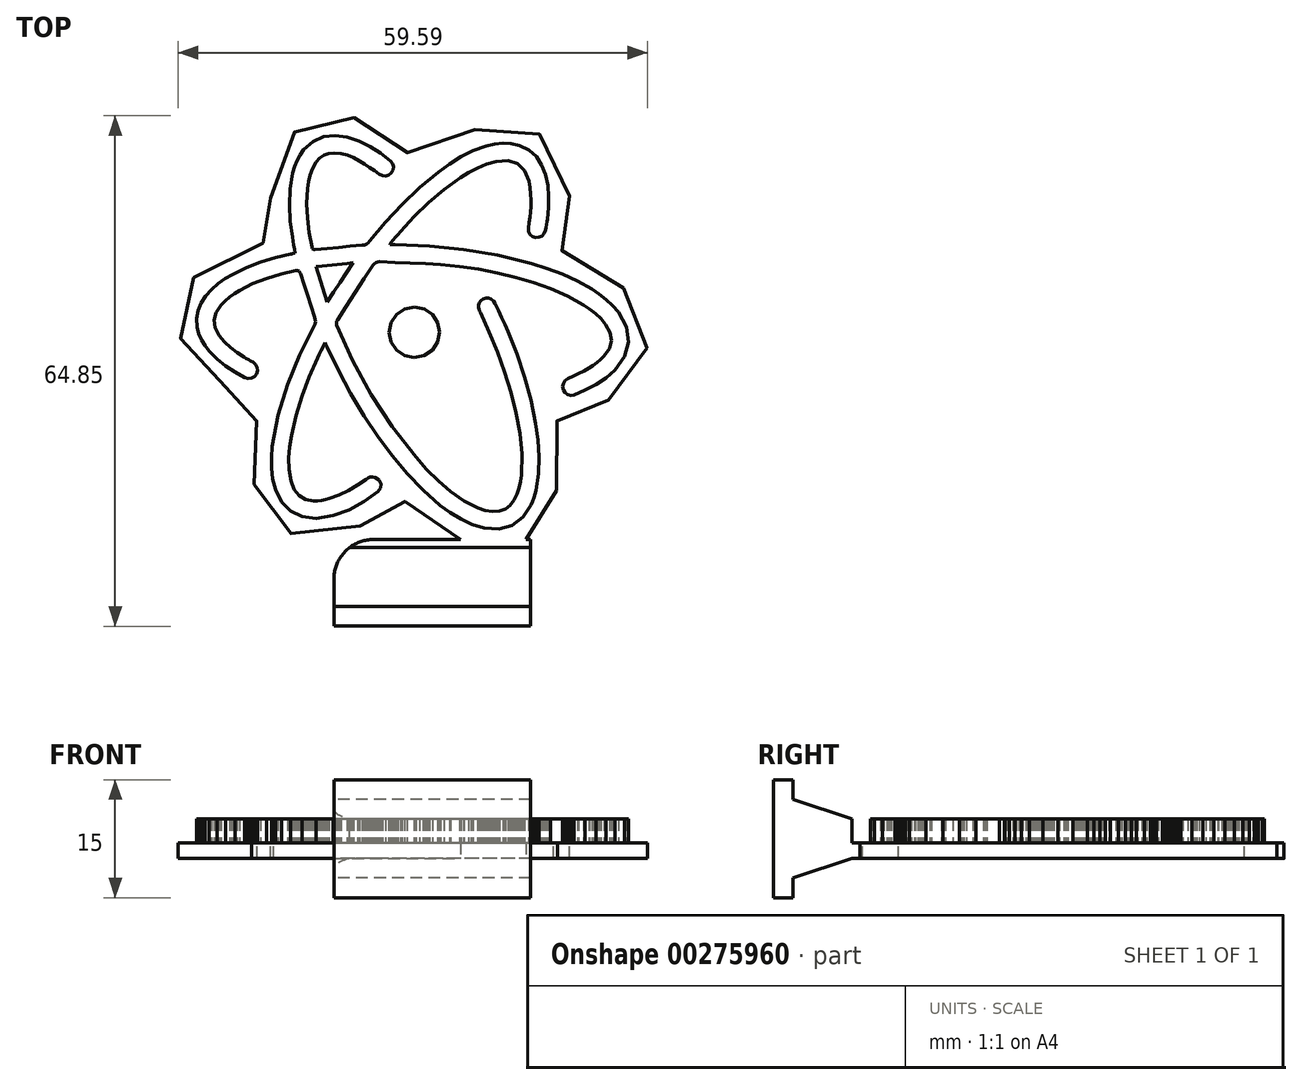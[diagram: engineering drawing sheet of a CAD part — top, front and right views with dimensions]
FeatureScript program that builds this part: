
annotation { "Feature Type Name" : "Feature", "Feature Type Description" : "" }
export const myFeature = defineFeature(function(context is Context, id is Id, definition is map)
    precondition{}
    {
        {
            var Q0;
            Q0=qCreatedBy(makeId("Top.planeOp"),FACE);
            var sketch = newSketch(context, id + "F0", { "sketchPlane" : qUnion([Q0])});
            skLineSegment(sketch, "E0", {"start": v(-11.14, -1.32) * mm, "end": v(-11.4, -1.85) * mm});
            skLineSegment(sketch, "E1", {"start": v(-11.4, -1.85) * mm, "end": v(-11.64, -2.35) * mm});
            skLineSegment(sketch, "E2", {"start": v(-11.64, -2.35) * mm, "end": v(-11.87, -2.83) * mm});
            skLineSegment(sketch, "E3", {"start": v(-11.87, -2.83) * mm, "end": v(-12.1, -3.3) * mm});
            skLineSegment(sketch, "E4", {"start": v(-12.1, -3.3) * mm, "end": v(-13.14, -5.69) * mm});
            skLineSegment(sketch, "E5", {"start": v(-13.14, -5.69) * mm, "end": v(-14.07, -8.11) * mm});
            skLineSegment(sketch, "E6", {"start": v(-14.07, -8.11) * mm, "end": v(-14.83, -10.59) * mm});
            skLineSegment(sketch, "E7", {"start": v(-14.83, -10.59) * mm, "end": v(-15.4, -13.13) * mm});
            skLineSegment(sketch, "E8", {"start": v(-15.4, -13.13) * mm, "end": v(-15.63, -14.56) * mm});
            skLineSegment(sketch, "E9", {"start": v(-15.63, -14.56) * mm, "end": v(-15.74, -16) * mm});
            skLineSegment(sketch, "E10", {"start": v(-15.74, -16) * mm, "end": v(-15.7, -17.44) * mm});
            skLineSegment(sketch, "E11", {"start": v(-15.7, -17.44) * mm, "end": v(-15.44, -18.87) * mm});
            skLineSegment(sketch, "E12", {"start": v(-15.44, -18.87) * mm, "end": v(-15.03, -19.96) * mm});
            skLineSegment(sketch, "E13", {"start": v(-15.03, -19.96) * mm, "end": v(-14.43, -20.74) * mm});
            skLineSegment(sketch, "E14", {"start": v(-14.43, -20.74) * mm, "end": v(-13.63, -21.24) * mm});
            skLineSegment(sketch, "E15", {"start": v(-13.63, -21.24) * mm, "end": v(-12.6, -21.43) * mm});
            skLineSegment(sketch, "E16", {"start": v(-12.6, -21.43) * mm, "end": v(-12.1, -21.43) * mm});
            skLineSegment(sketch, "E17", {"start": v(-12.1, -21.43) * mm, "end": v(-11.59, -21.37) * mm});
            skLineSegment(sketch, "E18", {"start": v(-11.59, -21.37) * mm, "end": v(-11.08, -21.27) * mm});
            skLineSegment(sketch, "E19", {"start": v(-11.08, -21.27) * mm, "end": v(-10.59, -21.14) * mm});
            skLineSegment(sketch, "E20", {"start": v(-10.59, -21.14) * mm, "end": v(-9.34, -20.7) * mm});
            skLineSegment(sketch, "E21", {"start": v(-9.34, -20.7) * mm, "end": v(-8.15, -20.12) * mm});
            skLineSegment(sketch, "E22", {"start": v(-8.15, -20.12) * mm, "end": v(-7.02, -19.44) * mm});
            skLineSegment(sketch, "E23", {"start": v(-7.02, -19.44) * mm, "end": v(-5.93, -18.7) * mm});
            skLineSegment(sketch, "E24", {"start": v(-5.93, -18.7) * mm, "end": v(-5.66, -18.53) * mm});
            skLineSegment(sketch, "E25", {"start": v(-5.66, -18.53) * mm, "end": v(-5.38, -18.42) * mm});
            skLineSegment(sketch, "E26", {"start": v(-5.38, -18.42) * mm, "end": v(-5.1, -18.39) * mm});
            skLineSegment(sketch, "E27", {"start": v(-5.1, -18.39) * mm, "end": v(-4.78, -18.46) * mm});
            skLineSegment(sketch, "E28", {"start": v(-4.78, -18.46) * mm, "end": v(-4.3, -18.8) * mm});
            skLineSegment(sketch, "E29", {"start": v(-4.3, -18.8) * mm, "end": v(-4.04, -19.28) * mm});
            skLineSegment(sketch, "E30", {"start": v(-4.04, -19.28) * mm, "end": v(-4.05, -19.81) * mm});
            skLineSegment(sketch, "E31", {"start": v(-4.05, -19.81) * mm, "end": v(-4.37, -20.26) * mm});
            skLineSegment(sketch, "E32", {"start": v(-4.37, -20.26) * mm, "end": v(-6.18, -21.52) * mm});
            skLineSegment(sketch, "E33", {"start": v(-6.18, -21.52) * mm, "end": v(-8.07, -22.57) * mm});
            skLineSegment(sketch, "E34", {"start": v(-8.07, -22.57) * mm, "end": v(-10.1, -23.32) * mm});
            skLineSegment(sketch, "E35", {"start": v(-10.1, -23.32) * mm, "end": v(-12.3, -23.63) * mm});
            skLineSegment(sketch, "E36", {"start": v(-12.3, -23.63) * mm, "end": v(-14.05, -23.43) * mm});
            skLineSegment(sketch, "E37", {"start": v(-14.05, -23.43) * mm, "end": v(-15.5, -22.73) * mm});
            skLineSegment(sketch, "E38", {"start": v(-15.5, -22.73) * mm, "end": v(-16.64, -21.57) * mm});
            skLineSegment(sketch, "E39", {"start": v(-16.64, -21.57) * mm, "end": v(-17.42, -19.98) * mm});
            skLineSegment(sketch, "E40", {"start": v(-17.42, -19.98) * mm, "end": v(-17.77, -18.63) * mm});
            skLineSegment(sketch, "E41", {"start": v(-17.77, -18.63) * mm, "end": v(-17.93, -17.27) * mm});
            skLineSegment(sketch, "E42", {"start": v(-17.93, -17.27) * mm, "end": v(-17.95, -15.9) * mm});
            skLineSegment(sketch, "E43", {"start": v(-17.95, -15.9) * mm, "end": v(-17.84, -14.52) * mm});
            skLineSegment(sketch, "E44", {"start": v(-17.84, -14.52) * mm, "end": v(-17.09, -10.5) * mm});
            skLineSegment(sketch, "E45", {"start": v(-17.09, -10.5) * mm, "end": v(-15.9, -6.63) * mm});
            skLineSegment(sketch, "E46", {"start": v(-15.9, -6.63) * mm, "end": v(-14.34, -2.89) * mm});
            skLineSegment(sketch, "E47", {"start": v(-14.34, -2.89) * mm, "end": v(-12.53, 0.76) * mm});
            skLineSegment(sketch, "E48", {"start": v(-12.53, 0.76) * mm, "end": v(-12.4, 1.06) * mm});
            skLineSegment(sketch, "E49", {"start": v(-12.4, 1.06) * mm, "end": v(-12.35, 1.35) * mm});
            skLineSegment(sketch, "E50", {"start": v(-12.35, 1.35) * mm, "end": v(-12.37, 1.64) * mm});
            skLineSegment(sketch, "E51", {"start": v(-12.37, 1.64) * mm, "end": v(-12.45, 1.95) * mm});
            skLineSegment(sketch, "E52", {"start": v(-12.45, 1.95) * mm, "end": v(-12.92, 3.32) * mm});
            skLineSegment(sketch, "E53", {"start": v(-12.92, 3.32) * mm, "end": v(-13.38, 4.7) * mm});
            skLineSegment(sketch, "E54", {"start": v(-13.38, 4.7) * mm, "end": v(-13.82, 6.07) * mm});
            skLineSegment(sketch, "E55", {"start": v(-13.82, 6.07) * mm, "end": v(-14.26, 7.45) * mm});
            skLineSegment(sketch, "E56", {"start": v(-14.26, 7.45) * mm, "end": v(-14.34, 7.66) * mm});
            skLineSegment(sketch, "E57", {"start": v(-14.34, 7.66) * mm, "end": v(-14.46, 7.8) * mm});
            skLineSegment(sketch, "E58", {"start": v(-14.46, 7.8) * mm, "end": v(-14.62, 7.84) * mm});
            skLineSegment(sketch, "E59", {"start": v(-14.62, 7.84) * mm, "end": v(-14.86, 7.81) * mm});
            skLineSegment(sketch, "E60", {"start": v(-14.86, 7.81) * mm, "end": v(-16.71, 7.37) * mm});
            skLineSegment(sketch, "E61", {"start": v(-16.71, 7.37) * mm, "end": v(-18.54, 6.84) * mm});
            skLineSegment(sketch, "E62", {"start": v(-18.54, 6.84) * mm, "end": v(-20.3, 6.16) * mm});
            skLineSegment(sketch, "E63", {"start": v(-20.3, 6.16) * mm, "end": v(-22, 5.29) * mm});
            skLineSegment(sketch, "E64", {"start": v(-22, 5.29) * mm, "end": v(-22.63, 4.89) * mm});
            skLineSegment(sketch, "E65", {"start": v(-22.63, 4.89) * mm, "end": v(-23.24, 4.44) * mm});
            skLineSegment(sketch, "E66", {"start": v(-23.24, 4.44) * mm, "end": v(-23.82, 3.96) * mm});
            skLineSegment(sketch, "E67", {"start": v(-23.82, 3.96) * mm, "end": v(-24.35, 3.44) * mm});
            skLineSegment(sketch, "E68", {"start": v(-24.35, 3.44) * mm, "end": v(-25, 2.53) * mm});
            skLineSegment(sketch, "E69", {"start": v(-25, 2.53) * mm, "end": v(-25.24, 1.57) * mm});
            skLineSegment(sketch, "E70", {"start": v(-25.24, 1.57) * mm, "end": v(-25.1, 0.59) * mm});
            skLineSegment(sketch, "E71", {"start": v(-25.1, 0.59) * mm, "end": v(-24.58, -0.42) * mm});
            skLineSegment(sketch, "E72", {"start": v(-24.58, -0.42) * mm, "end": v(-23.92, -1.25) * mm});
            skLineSegment(sketch, "E73", {"start": v(-23.92, -1.25) * mm, "end": v(-23.16, -1.96) * mm});
            skLineSegment(sketch, "E74", {"start": v(-23.16, -1.96) * mm, "end": v(-22.32, -2.58) * mm});
            skLineSegment(sketch, "E75", {"start": v(-22.32, -2.58) * mm, "end": v(-21.43, -3.15) * mm});
            skLineSegment(sketch, "E76", {"start": v(-21.43, -3.15) * mm, "end": v(-21.15, -3.32) * mm});
            skLineSegment(sketch, "E77", {"start": v(-21.15, -3.32) * mm, "end": v(-20.86, -3.48) * mm});
            skLineSegment(sketch, "E78", {"start": v(-20.86, -3.48) * mm, "end": v(-20.57, -3.64) * mm});
            skLineSegment(sketch, "E79", {"start": v(-20.57, -3.64) * mm, "end": v(-20.28, -3.8) * mm});
            skLineSegment(sketch, "E80", {"start": v(-20.28, -3.8) * mm, "end": v(-19.94, -4.1) * mm});
            skLineSegment(sketch, "E81", {"start": v(-19.94, -4.1) * mm, "end": v(-19.74, -4.48) * mm});
            skLineSegment(sketch, "E82", {"start": v(-19.74, -4.48) * mm, "end": v(-19.7, -4.89) * mm});
            skLineSegment(sketch, "E83", {"start": v(-19.7, -4.89) * mm, "end": v(-19.83, -5.3) * mm});
            skLineSegment(sketch, "E84", {"start": v(-19.83, -5.3) * mm, "end": v(-20.1, -5.64) * mm});
            skLineSegment(sketch, "E85", {"start": v(-20.1, -5.64) * mm, "end": v(-20.47, -5.83) * mm});
            skLineSegment(sketch, "E86", {"start": v(-20.47, -5.83) * mm, "end": v(-20.89, -5.88) * mm});
            skLineSegment(sketch, "E87", {"start": v(-20.89, -5.88) * mm, "end": v(-21.32, -5.75) * mm});
            skLineSegment(sketch, "E88", {"start": v(-21.32, -5.75) * mm, "end": v(-22.56, -5.06) * mm});
            skLineSegment(sketch, "E89", {"start": v(-22.56, -5.06) * mm, "end": v(-23.74, -4.3) * mm});
            skLineSegment(sketch, "E90", {"start": v(-23.74, -4.3) * mm, "end": v(-24.85, -3.41) * mm});
            skLineSegment(sketch, "E91", {"start": v(-24.85, -3.41) * mm, "end": v(-25.85, -2.4) * mm});
            skLineSegment(sketch, "E92", {"start": v(-25.85, -2.4) * mm, "end": v(-26.39, -1.72) * mm});
            skLineSegment(sketch, "E93", {"start": v(-26.39, -1.72) * mm, "end": v(-26.83, -0.98) * mm});
            skLineSegment(sketch, "E94", {"start": v(-26.83, -0.98) * mm, "end": v(-27.17, -0.2) * mm});
            skLineSegment(sketch, "E95", {"start": v(-27.17, -0.2) * mm, "end": v(-27.38, 0.66) * mm});
            skLineSegment(sketch, "E96", {"start": v(-27.38, 0.66) * mm, "end": v(-27.43, 1.73) * mm});
            skLineSegment(sketch, "E97", {"start": v(-27.43, 1.73) * mm, "end": v(-27.26, 2.74) * mm});
            skLineSegment(sketch, "E98", {"start": v(-27.26, 2.74) * mm, "end": v(-26.88, 3.69) * mm});
            skLineSegment(sketch, "E99", {"start": v(-26.88, 3.69) * mm, "end": v(-26.3, 4.59) * mm});
            skLineSegment(sketch, "E100", {"start": v(-26.3, 4.59) * mm, "end": v(-25.57, 5.43) * mm});
            skLineSegment(sketch, "E101", {"start": v(-25.57, 5.43) * mm, "end": v(-24.75, 6.15) * mm});
            skLineSegment(sketch, "E102", {"start": v(-24.75, 6.15) * mm, "end": v(-23.85, 6.8) * mm});
            skLineSegment(sketch, "E103", {"start": v(-23.85, 6.8) * mm, "end": v(-22.9, 7.35) * mm});
            skLineSegment(sketch, "E104", {"start": v(-22.9, 7.35) * mm, "end": v(-21.12, 8.2) * mm});
            skLineSegment(sketch, "E105", {"start": v(-21.12, 8.2) * mm, "end": v(-19.3, 8.9) * mm});
            skLineSegment(sketch, "E106", {"start": v(-19.3, 8.9) * mm, "end": v(-17.42, 9.47) * mm});
            skLineSegment(sketch, "E107", {"start": v(-17.42, 9.47) * mm, "end": v(-15.51, 9.92) * mm});
            skLineSegment(sketch, "E108", {"start": v(-15.51, 9.92) * mm, "end": v(-15.38, 9.95) * mm});
            skLineSegment(sketch, "E109", {"start": v(-15.38, 9.95) * mm, "end": v(-15.24, 9.99) * mm});
            skLineSegment(sketch, "E110", {"start": v(-15.24, 9.99) * mm, "end": v(-15.1, 10.03) * mm});
            skLineSegment(sketch, "E111", {"start": v(-15.1, 10.03) * mm, "end": v(-14.93, 10.07) * mm});
            skLineSegment(sketch, "E112", {"start": v(-14.93, 10.07) * mm, "end": v(-15.02, 10.58) * mm});
            skLineSegment(sketch, "E113", {"start": v(-15.02, 10.58) * mm, "end": v(-15.1, 11.08) * mm});
            skLineSegment(sketch, "E114", {"start": v(-15.1, 11.08) * mm, "end": v(-15.2, 11.58) * mm});
            skLineSegment(sketch, "E115", {"start": v(-15.2, 11.58) * mm, "end": v(-15.28, 12.09) * mm});
            skLineSegment(sketch, "E116", {"start": v(-15.28, 12.09) * mm, "end": v(-15.54, 14.13) * mm});
            skLineSegment(sketch, "E117", {"start": v(-15.54, 14.13) * mm, "end": v(-15.66, 16.17) * mm});
            skLineSegment(sketch, "E118", {"start": v(-15.66, 16.17) * mm, "end": v(-15.58, 18.2) * mm});
            skLineSegment(sketch, "E119", {"start": v(-15.58, 18.2) * mm, "end": v(-15.23, 20.24) * mm});
            skLineSegment(sketch, "E120", {"start": v(-15.23, 20.24) * mm, "end": v(-15, 21.03) * mm});
            skLineSegment(sketch, "E121", {"start": v(-15, 21.03) * mm, "end": v(-14.7, 21.79) * mm});
            skLineSegment(sketch, "E122", {"start": v(-14.7, 21.79) * mm, "end": v(-14.31, 22.5) * mm});
            skLineSegment(sketch, "E123", {"start": v(-14.31, 22.5) * mm, "end": v(-13.83, 23.18) * mm});
            skLineSegment(sketch, "E124", {"start": v(-13.83, 23.18) * mm, "end": v(-12.64, 24.24) * mm});
            skLineSegment(sketch, "E125", {"start": v(-12.64, 24.24) * mm, "end": v(-11.32, 24.83) * mm});
            skLineSegment(sketch, "E126", {"start": v(-11.32, 24.83) * mm, "end": v(-9.88, 25) * mm});
            skLineSegment(sketch, "E127", {"start": v(-9.88, 25) * mm, "end": v(-8.33, 24.79) * mm});
            skLineSegment(sketch, "E128", {"start": v(-8.33, 24.79) * mm, "end": v(-6.82, 24.29) * mm});
            skLineSegment(sketch, "E129", {"start": v(-6.82, 24.29) * mm, "end": v(-5.4, 23.59) * mm});
            skLineSegment(sketch, "E130", {"start": v(-5.4, 23.59) * mm, "end": v(-4.08, 22.73) * mm});
            skLineSegment(sketch, "E131", {"start": v(-4.08, 22.73) * mm, "end": v(-2.82, 21.76) * mm});
            skLineSegment(sketch, "E132", {"start": v(-2.82, 21.76) * mm, "end": v(-2.56, 21.42) * mm});
            skLineSegment(sketch, "E133", {"start": v(-2.56, 21.42) * mm, "end": v(-2.46, 21.02) * mm});
            skLineSegment(sketch, "E134", {"start": v(-2.46, 21.02) * mm, "end": v(-2.51, 20.6) * mm});
            skLineSegment(sketch, "E135", {"start": v(-2.51, 20.6) * mm, "end": v(-2.72, 20.24) * mm});
            skLineSegment(sketch, "E136", {"start": v(-2.72, 20.24) * mm, "end": v(-3.05, 19.97) * mm});
            skLineSegment(sketch, "E137", {"start": v(-3.05, 19.97) * mm, "end": v(-3.43, 19.86) * mm});
            skLineSegment(sketch, "E138", {"start": v(-3.43, 19.86) * mm, "end": v(-3.84, 19.9) * mm});
            skLineSegment(sketch, "E139", {"start": v(-3.84, 19.9) * mm, "end": v(-4.24, 20.08) * mm});
            skLineSegment(sketch, "E140", {"start": v(-4.24, 20.08) * mm, "end": v(-4.86, 20.51) * mm});
            skLineSegment(sketch, "E141", {"start": v(-4.86, 20.51) * mm, "end": v(-5.48, 20.94) * mm});
            skLineSegment(sketch, "E142", {"start": v(-5.48, 20.94) * mm, "end": v(-6.1, 21.36) * mm});
            skLineSegment(sketch, "E143", {"start": v(-6.1, 21.36) * mm, "end": v(-6.74, 21.76) * mm});
            skLineSegment(sketch, "E144", {"start": v(-6.74, 21.76) * mm, "end": v(-7.5, 22.16) * mm});
            skLineSegment(sketch, "E145", {"start": v(-7.5, 22.16) * mm, "end": v(-8.28, 22.48) * mm});
            skLineSegment(sketch, "E146", {"start": v(-8.28, 22.48) * mm, "end": v(-9.1, 22.69) * mm});
            skLineSegment(sketch, "E147", {"start": v(-9.1, 22.69) * mm, "end": v(-9.97, 22.76) * mm});
            skLineSegment(sketch, "E148", {"start": v(-9.97, 22.76) * mm, "end": v(-10.66, 22.7) * mm});
            skLineSegment(sketch, "E149", {"start": v(-10.66, 22.7) * mm, "end": v(-11.27, 22.47) * mm});
            skLineSegment(sketch, "E150", {"start": v(-11.27, 22.47) * mm, "end": v(-11.8, 22.1) * mm});
            skLineSegment(sketch, "E151", {"start": v(-11.8, 22.1) * mm, "end": v(-12.26, 21.58) * mm});
            skLineSegment(sketch, "E152", {"start": v(-12.26, 21.58) * mm, "end": v(-12.7, 20.8) * mm});
            skLineSegment(sketch, "E153", {"start": v(-12.7, 20.8) * mm, "end": v(-13.02, 19.98) * mm});
            skLineSegment(sketch, "E154", {"start": v(-13.02, 19.98) * mm, "end": v(-13.22, 19.12) * mm});
            skLineSegment(sketch, "E155", {"start": v(-13.22, 19.12) * mm, "end": v(-13.35, 18.24) * mm});
            skLineSegment(sketch, "E156", {"start": v(-13.35, 18.24) * mm, "end": v(-13.45, 16.36) * mm});
            skLineSegment(sketch, "E157", {"start": v(-13.45, 16.36) * mm, "end": v(-13.36, 14.5) * mm});
            skLineSegment(sketch, "E158", {"start": v(-13.36, 14.5) * mm, "end": v(-13.13, 12.65) * mm});
            skLineSegment(sketch, "E159", {"start": v(-13.13, 12.65) * mm, "end": v(-12.8, 10.8) * mm});
            skLineSegment(sketch, "E160", {"start": v(-12.8, 10.8) * mm, "end": v(-12.75, 10.64) * mm});
            skLineSegment(sketch, "E161", {"start": v(-12.75, 10.64) * mm, "end": v(-12.67, 10.54) * mm});
            skLineSegment(sketch, "E162", {"start": v(-12.67, 10.54) * mm, "end": v(-12.55, 10.49) * mm});
            skLineSegment(sketch, "E163", {"start": v(-12.55, 10.49) * mm, "end": v(-12.38, 10.48) * mm});
            skLineSegment(sketch, "E164", {"start": v(-12.38, 10.48) * mm, "end": v(-10.9, 10.63) * mm});
            skLineSegment(sketch, "E165", {"start": v(-10.9, 10.63) * mm, "end": v(-9.4, 10.78) * mm});
            skLineSegment(sketch, "E166", {"start": v(-9.4, 10.78) * mm, "end": v(-7.92, 10.91) * mm});
            skLineSegment(sketch, "E167", {"start": v(-7.92, 10.91) * mm, "end": v(-6.43, 11.04) * mm});
            skLineSegment(sketch, "E168", {"start": v(-6.43, 11.04) * mm, "end": v(-6.14, 11.1) * mm});
            skLineSegment(sketch, "E169", {"start": v(-6.14, 11.1) * mm, "end": v(-5.88, 11.2) * mm});
            skLineSegment(sketch, "E170", {"start": v(-5.88, 11.2) * mm, "end": v(-5.66, 11.35) * mm});
            skLineSegment(sketch, "E171", {"start": v(-5.66, 11.35) * mm, "end": v(-5.45, 11.57) * mm});
            skLineSegment(sketch, "E172", {"start": v(-5.45, 11.57) * mm, "end": v(-3.47, 13.97) * mm});
            skLineSegment(sketch, "E173", {"start": v(-3.47, 13.97) * mm, "end": v(-1.37, 16.24) * mm});
            skLineSegment(sketch, "E174", {"start": v(-1.37, 16.24) * mm, "end": v(0.87, 18.38) * mm});
            skLineSegment(sketch, "E175", {"start": v(0.87, 18.38) * mm, "end": v(3.27, 20.36) * mm});
            skLineSegment(sketch, "E176", {"start": v(3.27, 20.36) * mm, "end": v(4.68, 21.37) * mm});
            skLineSegment(sketch, "E177", {"start": v(4.68, 21.37) * mm, "end": v(6.15, 22.28) * mm});
            skLineSegment(sketch, "E178", {"start": v(6.15, 22.28) * mm, "end": v(7.7, 23.05) * mm});
            skLineSegment(sketch, "E179", {"start": v(7.7, 23.05) * mm, "end": v(9.33, 23.65) * mm});
            skLineSegment(sketch, "E180", {"start": v(9.33, 23.65) * mm, "end": v(10.4, 23.9) * mm});
            skLineSegment(sketch, "E181", {"start": v(10.4, 23.9) * mm, "end": v(11.46, 24.03) * mm});
            skLineSegment(sketch, "E182", {"start": v(11.46, 24.03) * mm, "end": v(12.52, 23.98) * mm});
            skLineSegment(sketch, "E183", {"start": v(12.52, 23.98) * mm, "end": v(13.59, 23.72) * mm});
            skLineSegment(sketch, "E184", {"start": v(13.59, 23.72) * mm, "end": v(14.78, 23.12) * mm});
            skLineSegment(sketch, "E185", {"start": v(14.78, 23.12) * mm, "end": v(15.7, 22.28) * mm});
            skLineSegment(sketch, "E186", {"start": v(15.7, 22.28) * mm, "end": v(16.39, 21.24) * mm});
            skLineSegment(sketch, "E187", {"start": v(16.39, 21.24) * mm, "end": v(16.87, 20) * mm});
            skLineSegment(sketch, "E188", {"start": v(16.87, 20) * mm, "end": v(17.16, 18.62) * mm});
            skLineSegment(sketch, "E189", {"start": v(17.16, 18.62) * mm, "end": v(17.27, 17.22) * mm});
            skLineSegment(sketch, "E190", {"start": v(17.27, 17.22) * mm, "end": v(17.23, 15.8) * mm});
            skLineSegment(sketch, "E191", {"start": v(17.23, 15.8) * mm, "end": v(17.1, 14.4) * mm});
            skLineSegment(sketch, "E192", {"start": v(17.1, 14.4) * mm, "end": v(17.06, 14.04) * mm});
            skLineSegment(sketch, "E193", {"start": v(17.06, 14.04) * mm, "end": v(17, 13.68) * mm});
            skLineSegment(sketch, "E194", {"start": v(17, 13.68) * mm, "end": v(16.94, 13.32) * mm});
            skLineSegment(sketch, "E195", {"start": v(16.94, 13.32) * mm, "end": v(16.87, 12.96) * mm});
            skLineSegment(sketch, "E196", {"start": v(16.87, 12.96) * mm, "end": v(16.71, 12.53) * mm});
            skLineSegment(sketch, "E197", {"start": v(16.71, 12.53) * mm, "end": v(16.44, 12.23) * mm});
            skLineSegment(sketch, "E198", {"start": v(16.44, 12.23) * mm, "end": v(16.07, 12.06) * mm});
            skLineSegment(sketch, "E199", {"start": v(16.07, 12.06) * mm, "end": v(15.62, 12.04) * mm});
            skLineSegment(sketch, "E200", {"start": v(15.62, 12.04) * mm, "end": v(15.22, 12.17) * mm});
            skLineSegment(sketch, "E201", {"start": v(15.22, 12.17) * mm, "end": v(14.92, 12.42) * mm});
            skLineSegment(sketch, "E202", {"start": v(14.92, 12.42) * mm, "end": v(14.74, 12.79) * mm});
            skLineSegment(sketch, "E203", {"start": v(14.74, 12.79) * mm, "end": v(14.7, 13.24) * mm});
            skLineSegment(sketch, "E204", {"start": v(14.7, 13.24) * mm, "end": v(14.79, 13.92) * mm});
            skLineSegment(sketch, "E205", {"start": v(14.79, 13.92) * mm, "end": v(14.89, 14.6) * mm});
            skLineSegment(sketch, "E206", {"start": v(14.89, 14.6) * mm, "end": v(14.97, 15.28) * mm});
            skLineSegment(sketch, "E207", {"start": v(14.97, 15.28) * mm, "end": v(15, 15.96) * mm});
            skLineSegment(sketch, "E208", {"start": v(15, 15.96) * mm, "end": v(15, 16.76) * mm});
            skLineSegment(sketch, "E209", {"start": v(15, 16.76) * mm, "end": v(14.98, 17.57) * mm});
            skLineSegment(sketch, "E210", {"start": v(14.98, 17.57) * mm, "end": v(14.9, 18.38) * mm});
            skLineSegment(sketch, "E211", {"start": v(14.9, 18.38) * mm, "end": v(14.77, 19.17) * mm});
            skLineSegment(sketch, "E212", {"start": v(14.77, 19.17) * mm, "end": v(14.24, 20.54) * mm});
            skLineSegment(sketch, "E213", {"start": v(14.24, 20.54) * mm, "end": v(13.34, 21.42) * mm});
            skLineSegment(sketch, "E214", {"start": v(13.34, 21.42) * mm, "end": v(12.12, 21.8) * mm});
            skLineSegment(sketch, "E215", {"start": v(12.12, 21.8) * mm, "end": v(10.6, 21.7) * mm});
            skLineSegment(sketch, "E216", {"start": v(10.6, 21.7) * mm, "end": v(9.39, 21.34) * mm});
            skLineSegment(sketch, "E217", {"start": v(9.39, 21.34) * mm, "end": v(8.23, 20.87) * mm});
            skLineSegment(sketch, "E218", {"start": v(8.23, 20.87) * mm, "end": v(7.13, 20.28) * mm});
            skLineSegment(sketch, "E219", {"start": v(7.13, 20.28) * mm, "end": v(6.06, 19.62) * mm});
            skLineSegment(sketch, "E220", {"start": v(6.06, 19.62) * mm, "end": v(3.98, 18.11) * mm});
            skLineSegment(sketch, "E221", {"start": v(3.98, 18.11) * mm, "end": v(2.03, 16.45) * mm});
            skLineSegment(sketch, "E222", {"start": v(2.03, 16.45) * mm, "end": v(0.19, 14.67) * mm});
            skLineSegment(sketch, "E223", {"start": v(0.19, 14.67) * mm, "end": v(-1.56, 12.78) * mm});
            skLineSegment(sketch, "E224", {"start": v(-1.56, 12.78) * mm, "end": v(-1.88, 12.42) * mm});
            skLineSegment(sketch, "E225", {"start": v(-1.88, 12.42) * mm, "end": v(-2.19, 12.06) * mm});
            skLineSegment(sketch, "E226", {"start": v(-2.19, 12.06) * mm, "end": v(-2.5, 11.7) * mm});
            skLineSegment(sketch, "E227", {"start": v(-2.5, 11.7) * mm, "end": v(-2.8, 11.32) * mm});
            skLineSegment(sketch, "E228", {"start": v(-2.8, 11.32) * mm, "end": v(-2.82, 11.3) * mm});
            skLineSegment(sketch, "E229", {"start": v(-2.82, 11.3) * mm, "end": v(-2.83, 11.26) * mm});
            skLineSegment(sketch, "E230", {"start": v(-2.83, 11.26) * mm, "end": v(-2.84, 11.2) * mm});
            skLineSegment(sketch, "E231", {"start": v(-2.84, 11.2) * mm, "end": v(-2.86, 11.12) * mm});
            skLineSegment(sketch, "E232", {"start": v(-2.86, 11.12) * mm, "end": v(-2.71, 11.12) * mm});
            skLineSegment(sketch, "E233", {"start": v(-2.71, 11.12) * mm, "end": v(-2.56, 11.12) * mm});
            skLineSegment(sketch, "E234", {"start": v(-2.56, 11.12) * mm, "end": v(-2.41, 11.12) * mm});
            skLineSegment(sketch, "E235", {"start": v(-2.41, 11.12) * mm, "end": v(-2.26, 11.12) * mm});
            skLineSegment(sketch, "E236", {"start": v(-2.26, 11.12) * mm, "end": v(2.13, 10.95) * mm});
            skLineSegment(sketch, "E237", {"start": v(2.13, 10.95) * mm, "end": v(6.48, 10.52) * mm});
            skLineSegment(sketch, "E238", {"start": v(6.48, 10.52) * mm, "end": v(10.8, 9.78) * mm});
            skLineSegment(sketch, "E239", {"start": v(10.8, 9.78) * mm, "end": v(15.07, 8.73) * mm});
            skLineSegment(sketch, "E240", {"start": v(15.07, 8.73) * mm, "end": v(17.07, 8.1) * mm});
            skLineSegment(sketch, "E241", {"start": v(17.07, 8.1) * mm, "end": v(19.03, 7.36) * mm});
            skLineSegment(sketch, "E242", {"start": v(19.03, 7.36) * mm, "end": v(20.93, 6.49) * mm});
            skLineSegment(sketch, "E243", {"start": v(20.93, 6.49) * mm, "end": v(22.76, 5.46) * mm});
            skLineSegment(sketch, "E244", {"start": v(22.76, 5.46) * mm, "end": v(23.7, 4.84) * mm});
            skLineSegment(sketch, "E245", {"start": v(23.7, 4.84) * mm, "end": v(24.58, 4.15) * mm});
            skLineSegment(sketch, "E246", {"start": v(24.58, 4.15) * mm, "end": v(25.4, 3.4) * mm});
            skLineSegment(sketch, "E247", {"start": v(25.4, 3.4) * mm, "end": v(26.13, 2.55) * mm});
            skLineSegment(sketch, "E248", {"start": v(26.13, 2.55) * mm, "end": v(27.16, 0.67) * mm});
            skLineSegment(sketch, "E249", {"start": v(27.16, 0.67) * mm, "end": v(27.43, -1.23) * mm});
            skLineSegment(sketch, "E250", {"start": v(27.43, -1.23) * mm, "end": v(26.94, -3.09) * mm});
            skLineSegment(sketch, "E251", {"start": v(26.94, -3.09) * mm, "end": v(25.69, -4.82) * mm});
            skLineSegment(sketch, "E252", {"start": v(25.69, -4.82) * mm, "end": v(24.53, -5.83) * mm});
            skLineSegment(sketch, "E253", {"start": v(24.53, -5.83) * mm, "end": v(23.26, -6.67) * mm});
            skLineSegment(sketch, "E254", {"start": v(23.26, -6.67) * mm, "end": v(21.91, -7.37) * mm});
            skLineSegment(sketch, "E255", {"start": v(21.91, -7.37) * mm, "end": v(20.5, -7.95) * mm});
            skLineSegment(sketch, "E256", {"start": v(20.5, -7.95) * mm, "end": v(20.08, -8.02) * mm});
            skLineSegment(sketch, "E257", {"start": v(20.08, -8.02) * mm, "end": v(19.7, -7.92) * mm});
            skLineSegment(sketch, "E258", {"start": v(19.7, -7.92) * mm, "end": v(19.37, -7.68) * mm});
            skLineSegment(sketch, "E259", {"start": v(19.37, -7.68) * mm, "end": v(19.14, -7.34) * mm});
            skLineSegment(sketch, "E260", {"start": v(19.14, -7.34) * mm, "end": v(19.06, -6.9) * mm});
            skLineSegment(sketch, "E261", {"start": v(19.06, -6.9) * mm, "end": v(19.14, -6.5) * mm});
            skLineSegment(sketch, "E262", {"start": v(19.14, -6.5) * mm, "end": v(19.37, -6.15) * mm});
            skLineSegment(sketch, "E263", {"start": v(19.37, -6.15) * mm, "end": v(19.75, -5.89) * mm});
            skLineSegment(sketch, "E264", {"start": v(19.75, -5.89) * mm, "end": v(20.42, -5.57) * mm});
            skLineSegment(sketch, "E265", {"start": v(20.42, -5.57) * mm, "end": v(21.09, -5.26) * mm});
            skLineSegment(sketch, "E266", {"start": v(21.09, -5.26) * mm, "end": v(21.75, -4.94) * mm});
            skLineSegment(sketch, "E267", {"start": v(21.75, -4.94) * mm, "end": v(22.4, -4.57) * mm});
            skLineSegment(sketch, "E268", {"start": v(22.4, -4.57) * mm, "end": v(22.9, -4.24) * mm});
            skLineSegment(sketch, "E269", {"start": v(22.9, -4.24) * mm, "end": v(23.4, -3.87) * mm});
            skLineSegment(sketch, "E270", {"start": v(23.4, -3.87) * mm, "end": v(23.87, -3.47) * mm});
            skLineSegment(sketch, "E271", {"start": v(23.87, -3.47) * mm, "end": v(24.3, -3.04) * mm});
            skLineSegment(sketch, "E272", {"start": v(24.3, -3.04) * mm, "end": v(24.98, -2.08) * mm});
            skLineSegment(sketch, "E273", {"start": v(24.98, -2.08) * mm, "end": v(25.23, -1.09) * mm});
            skLineSegment(sketch, "E274", {"start": v(25.23, -1.09) * mm, "end": v(25.08, -0.06) * mm});
            skLineSegment(sketch, "E275", {"start": v(25.08, -0.06) * mm, "end": v(24.53, 0.98) * mm});
            skLineSegment(sketch, "E276", {"start": v(24.53, 0.98) * mm, "end": v(23.92, 1.72) * mm});
            skLineSegment(sketch, "E277", {"start": v(23.92, 1.72) * mm, "end": v(23.24, 2.36) * mm});
            skLineSegment(sketch, "E278", {"start": v(23.24, 2.36) * mm, "end": v(22.5, 2.94) * mm});
            skLineSegment(sketch, "E279", {"start": v(22.5, 2.94) * mm, "end": v(21.7, 3.46) * mm});
            skLineSegment(sketch, "E280", {"start": v(21.7, 3.46) * mm, "end": v(19.66, 4.6) * mm});
            skLineSegment(sketch, "E281", {"start": v(19.66, 4.6) * mm, "end": v(17.54, 5.52) * mm});
            skLineSegment(sketch, "E282", {"start": v(17.54, 5.52) * mm, "end": v(15.35, 6.3) * mm});
            skLineSegment(sketch, "E283", {"start": v(15.35, 6.3) * mm, "end": v(13.11, 6.94) * mm});
            skLineSegment(sketch, "E284", {"start": v(13.11, 6.94) * mm, "end": v(10.75, 7.52) * mm});
            skLineSegment(sketch, "E285", {"start": v(10.75, 7.52) * mm, "end": v(8.37, 8) * mm});
            skLineSegment(sketch, "E286", {"start": v(8.37, 8) * mm, "end": v(5.98, 8.35) * mm});
            skLineSegment(sketch, "E287", {"start": v(5.98, 8.35) * mm, "end": v(3.56, 8.59) * mm});
            skLineSegment(sketch, "E288", {"start": v(3.56, 8.59) * mm, "end": v(1.63, 8.7) * mm});
            skLineSegment(sketch, "E289", {"start": v(1.63, 8.7) * mm, "end": v(-0.3, 8.79) * mm});
            skLineSegment(sketch, "E290", {"start": v(-0.3, 8.79) * mm, "end": v(-2.25, 8.86) * mm});
            skLineSegment(sketch, "E291", {"start": v(-2.25, 8.86) * mm, "end": v(-4.18, 8.95) * mm});
            skLineSegment(sketch, "E292", {"start": v(-4.18, 8.95) * mm, "end": v(-4.44, 8.93) * mm});
            skLineSegment(sketch, "E293", {"start": v(-4.44, 8.93) * mm, "end": v(-4.66, 8.87) * mm});
            skLineSegment(sketch, "E294", {"start": v(-4.66, 8.87) * mm, "end": v(-4.85, 8.74) * mm});
            skLineSegment(sketch, "E295", {"start": v(-4.85, 8.74) * mm, "end": v(-5.02, 8.53) * mm});
            skLineSegment(sketch, "E296", {"start": v(-5.02, 8.53) * mm, "end": v(-6.16, 6.78) * mm});
            skLineSegment(sketch, "E297", {"start": v(-6.16, 6.78) * mm, "end": v(-7.3, 5.04) * mm});
            skLineSegment(sketch, "E298", {"start": v(-7.3, 5.04) * mm, "end": v(-8.43, 3.29) * mm});
            skLineSegment(sketch, "E299", {"start": v(-8.43, 3.29) * mm, "end": v(-9.57, 1.54) * mm});
            skLineSegment(sketch, "E300", {"start": v(-9.57, 1.54) * mm, "end": v(-9.64, 1.39) * mm});
            skLineSegment(sketch, "E301", {"start": v(-9.64, 1.39) * mm, "end": v(-9.68, 1.21) * mm});
            skLineSegment(sketch, "E302", {"start": v(-9.68, 1.21) * mm, "end": v(-9.68, 1.04) * mm});
            skLineSegment(sketch, "E303", {"start": v(-9.68, 1.04) * mm, "end": v(-9.65, 0.88) * mm});
            skLineSegment(sketch, "E304", {"start": v(-9.65, 0.88) * mm, "end": v(-7.6, -3.59) * mm});
            skLineSegment(sketch, "E305", {"start": v(-7.6, -3.59) * mm, "end": v(-5.27, -7.89) * mm});
            skLineSegment(sketch, "E306", {"start": v(-5.27, -7.89) * mm, "end": v(-2.61, -11.99) * mm});
            skLineSegment(sketch, "E307", {"start": v(-2.61, -11.99) * mm, "end": v(0.4, -15.87) * mm});
            skLineSegment(sketch, "E308", {"start": v(0.4, -15.87) * mm, "end": v(1.8, -17.42) * mm});
            skLineSegment(sketch, "E309", {"start": v(1.8, -17.42) * mm, "end": v(3.26, -18.89) * mm});
            skLineSegment(sketch, "E310", {"start": v(3.26, -18.89) * mm, "end": v(4.83, -20.23) * mm});
            skLineSegment(sketch, "E311", {"start": v(4.83, -20.23) * mm, "end": v(6.54, -21.42) * mm});
            skLineSegment(sketch, "E312", {"start": v(6.54, -21.42) * mm, "end": v(7.4, -21.92) * mm});
            skLineSegment(sketch, "E313", {"start": v(7.4, -21.92) * mm, "end": v(8.27, -22.33) * mm});
            skLineSegment(sketch, "E314", {"start": v(8.27, -22.33) * mm, "end": v(9.2, -22.63) * mm});
            skLineSegment(sketch, "E315", {"start": v(9.2, -22.63) * mm, "end": v(10.18, -22.79) * mm});
            skLineSegment(sketch, "E316", {"start": v(10.18, -22.79) * mm, "end": v(11.03, -22.74) * mm});
            skLineSegment(sketch, "E317", {"start": v(11.03, -22.74) * mm, "end": v(11.77, -22.47) * mm});
            skLineSegment(sketch, "E318", {"start": v(11.77, -22.47) * mm, "end": v(12.4, -22) * mm});
            skLineSegment(sketch, "E319", {"start": v(12.4, -22) * mm, "end": v(12.9, -21.32) * mm});
            skLineSegment(sketch, "E320", {"start": v(12.9, -21.32) * mm, "end": v(13.27, -20.57) * mm});
            skLineSegment(sketch, "E321", {"start": v(13.27, -20.57) * mm, "end": v(13.53, -19.78) * mm});
            skLineSegment(sketch, "E322", {"start": v(13.53, -19.78) * mm, "end": v(13.7, -18.97) * mm});
            skLineSegment(sketch, "E323", {"start": v(13.7, -18.97) * mm, "end": v(13.8, -18.14) * mm});
            skLineSegment(sketch, "E324", {"start": v(13.8, -18.14) * mm, "end": v(13.87, -15.47) * mm});
            skLineSegment(sketch, "E325", {"start": v(13.87, -15.47) * mm, "end": v(13.62, -12.84) * mm});
            skLineSegment(sketch, "E326", {"start": v(13.62, -12.84) * mm, "end": v(13.14, -10.24) * mm});
            skLineSegment(sketch, "E327", {"start": v(13.14, -10.24) * mm, "end": v(12.49, -7.66) * mm});
            skLineSegment(sketch, "E328", {"start": v(12.49, -7.66) * mm, "end": v(11.7, -5.06) * mm});
            skLineSegment(sketch, "E329", {"start": v(11.7, -5.06) * mm, "end": v(10.76, -2.5) * mm});
            skLineSegment(sketch, "E330", {"start": v(10.76, -2.5) * mm, "end": v(9.73, 0.02) * mm});
            skLineSegment(sketch, "E331", {"start": v(9.73, 0.02) * mm, "end": v(8.6, 2.5) * mm});
            skLineSegment(sketch, "E332", {"start": v(8.6, 2.5) * mm, "end": v(8.5, 2.7) * mm});
            skLineSegment(sketch, "E333", {"start": v(8.5, 2.7) * mm, "end": v(8.43, 2.92) * mm});
            skLineSegment(sketch, "E334", {"start": v(8.43, 2.92) * mm, "end": v(8.39, 3.14) * mm});
            skLineSegment(sketch, "E335", {"start": v(8.39, 3.14) * mm, "end": v(8.38, 3.36) * mm});
            skLineSegment(sketch, "E336", {"start": v(8.38, 3.36) * mm, "end": v(8.46, 3.72) * mm});
            skLineSegment(sketch, "E337", {"start": v(8.46, 3.72) * mm, "end": v(8.67, 4) * mm});
            skLineSegment(sketch, "E338", {"start": v(8.67, 4) * mm, "end": v(8.96, 4.21) * mm});
            skLineSegment(sketch, "E339", {"start": v(8.96, 4.21) * mm, "end": v(9.32, 4.32) * mm});
            skLineSegment(sketch, "E340", {"start": v(9.32, 4.32) * mm, "end": v(9.66, 4.32) * mm});
            skLineSegment(sketch, "E341", {"start": v(9.66, 4.32) * mm, "end": v(9.98, 4.2) * mm});
            skLineSegment(sketch, "E342", {"start": v(9.98, 4.2) * mm, "end": v(10.26, 3.98) * mm});
            skLineSegment(sketch, "E343", {"start": v(10.26, 3.98) * mm, "end": v(10.47, 3.67) * mm});
            skLineSegment(sketch, "E344", {"start": v(10.47, 3.67) * mm, "end": v(10.89, 2.77) * mm});
            skLineSegment(sketch, "E345", {"start": v(10.89, 2.77) * mm, "end": v(11.3, 1.87) * mm});
            skLineSegment(sketch, "E346", {"start": v(11.3, 1.87) * mm, "end": v(11.71, 0.96) * mm});
            skLineSegment(sketch, "E347", {"start": v(11.71, 0.96) * mm, "end": v(12.1, 0.05) * mm});
            skLineSegment(sketch, "E348", {"start": v(12.1, 0.05) * mm, "end": v(13.23, -2.79) * mm});
            skLineSegment(sketch, "E349", {"start": v(13.23, -2.79) * mm, "end": v(14.21, -5.67) * mm});
            skLineSegment(sketch, "E350", {"start": v(14.21, -5.67) * mm, "end": v(15.02, -8.61) * mm});
            skLineSegment(sketch, "E351", {"start": v(15.02, -8.61) * mm, "end": v(15.63, -11.6) * mm});
            skLineSegment(sketch, "E352", {"start": v(15.63, -11.6) * mm, "end": v(15.93, -13.72) * mm});
            skLineSegment(sketch, "E353", {"start": v(15.93, -13.72) * mm, "end": v(16.08, -15.84) * mm});
            skLineSegment(sketch, "E354", {"start": v(16.08, -15.84) * mm, "end": v(16.01, -17.96) * mm});
            skLineSegment(sketch, "E355", {"start": v(16.01, -17.96) * mm, "end": v(15.68, -20.08) * mm});
            skLineSegment(sketch, "E356", {"start": v(15.68, -20.08) * mm, "end": v(15.55, -20.55) * mm});
            skLineSegment(sketch, "E357", {"start": v(15.55, -20.55) * mm, "end": v(15.4, -21.02) * mm});
            skLineSegment(sketch, "E358", {"start": v(15.4, -21.02) * mm, "end": v(15.24, -21.48) * mm});
            skLineSegment(sketch, "E359", {"start": v(15.24, -21.48) * mm, "end": v(15.04, -21.93) * mm});
            skLineSegment(sketch, "E360", {"start": v(15.04, -21.93) * mm, "end": v(14.01, -23.5) * mm});
            skLineSegment(sketch, "E361", {"start": v(14.01, -23.5) * mm, "end": v(12.62, -24.53) * mm});
            skLineSegment(sketch, "E362", {"start": v(12.62, -24.53) * mm, "end": v(10.95, -25) * mm});
            skLineSegment(sketch, "E363", {"start": v(10.95, -25) * mm, "end": v(9.08, -24.88) * mm});
            skLineSegment(sketch, "E364", {"start": v(9.08, -24.88) * mm, "end": v(7.55, -24.42) * mm});
            skLineSegment(sketch, "E365", {"start": v(7.55, -24.42) * mm, "end": v(6.12, -23.75) * mm});
            skLineSegment(sketch, "E366", {"start": v(6.12, -23.75) * mm, "end": v(4.78, -22.93) * mm});
            skLineSegment(sketch, "E367", {"start": v(4.78, -22.93) * mm, "end": v(3.5, -21.99) * mm});
            skLineSegment(sketch, "E368", {"start": v(3.5, -21.99) * mm, "end": v(1.3, -20.07) * mm});
            skLineSegment(sketch, "E369", {"start": v(1.3, -20.07) * mm, "end": v(-0.71, -17.98) * mm});
            skLineSegment(sketch, "E370", {"start": v(-0.71, -17.98) * mm, "end": v(-2.57, -15.75) * mm});
            skLineSegment(sketch, "E371", {"start": v(-2.57, -15.75) * mm, "end": v(-4.31, -13.4) * mm});
            skLineSegment(sketch, "E372", {"start": v(-4.31, -13.4) * mm, "end": v(-6.16, -10.65) * mm});
            skLineSegment(sketch, "E373", {"start": v(-6.16, -10.65) * mm, "end": v(-7.87, -7.81) * mm});
            skLineSegment(sketch, "E374", {"start": v(-7.87, -7.81) * mm, "end": v(-9.43, -4.89) * mm});
            skLineSegment(sketch, "E375", {"start": v(-9.43, -4.89) * mm, "end": v(-10.86, -1.9) * mm});
            skLineSegment(sketch, "E376", {"start": v(-10.86, -1.9) * mm, "end": v(-10.92, -1.78) * mm});
            skLineSegment(sketch, "E377", {"start": v(-10.92, -1.78) * mm, "end": v(-10.98, -1.65) * mm});
            skLineSegment(sketch, "E378", {"start": v(-10.98, -1.65) * mm, "end": v(-11.05, -1.5) * mm});
            skLineSegment(sketch, "E379", {"start": v(-11.05, -1.5) * mm, "end": v(-11.14, -1.32) * mm});
            skLineSegment(sketch, "E380", {"start": v(-12.25, 8.32) * mm, "end": v(-11.9, 7.2) * mm});
            skLineSegment(sketch, "E381", {"start": v(-11.9, 7.2) * mm, "end": v(-11.55, 6.08) * mm});
            skLineSegment(sketch, "E382", {"start": v(-11.55, 6.08) * mm, "end": v(-11.2, 4.97) * mm});
            skLineSegment(sketch, "E383", {"start": v(-11.2, 4.97) * mm, "end": v(-10.85, 3.85) * mm});
            skLineSegment(sketch, "E384", {"start": v(-10.85, 3.85) * mm, "end": v(-10.03, 5.1) * mm});
            skLineSegment(sketch, "E385", {"start": v(-10.03, 5.1) * mm, "end": v(-9.22, 6.33) * mm});
            skLineSegment(sketch, "E386", {"start": v(-9.22, 6.33) * mm, "end": v(-8.42, 7.57) * mm});
            skLineSegment(sketch, "E387", {"start": v(-8.42, 7.57) * mm, "end": v(-7.6, 8.82) * mm});
            skLineSegment(sketch, "E388", {"start": v(-7.6, 8.82) * mm, "end": v(-8.32, 8.74) * mm});
            skLineSegment(sketch, "E389", {"start": v(-8.32, 8.74) * mm, "end": v(-9.92, 8.57) * mm});
            skLineSegment(sketch, "E390", {"start": v(-9.92, 8.57) * mm, "end": v(-11.53, 8.4) * mm});
            skLineSegment(sketch, "E391", {"start": v(-11.53, 8.4) * mm, "end": v(-12.25, 8.32) * mm});
            skLineSegment(sketch, "E392", {"start": v(0.2, -3.2) * mm, "end": v(-1.04, -2.95) * mm});
            skLineSegment(sketch, "E393", {"start": v(-1.04, -2.95) * mm, "end": v(-2.06, -2.27) * mm});
            skLineSegment(sketch, "E394", {"start": v(-2.06, -2.27) * mm, "end": v(-2.74, -1.26) * mm});
            skLineSegment(sketch, "E395", {"start": v(-2.74, -1.26) * mm, "end": v(-3, -0.02) * mm});
            skLineSegment(sketch, "E396", {"start": v(-3, -0.02) * mm, "end": v(-2.74, 1.23) * mm});
            skLineSegment(sketch, "E397", {"start": v(-2.74, 1.23) * mm, "end": v(-2.05, 2.24) * mm});
            skLineSegment(sketch, "E398", {"start": v(-2.05, 2.24) * mm, "end": v(-1.02, 2.93) * mm});
            skLineSegment(sketch, "E399", {"start": v(-1.02, 2.93) * mm, "end": v(0.24, 3.17) * mm});
            skLineSegment(sketch, "E400", {"start": v(0.24, 3.17) * mm, "end": v(1.48, 2.92) * mm});
            skLineSegment(sketch, "E401", {"start": v(1.48, 2.92) * mm, "end": v(2.5, 2.24) * mm});
            skLineSegment(sketch, "E402", {"start": v(2.5, 2.24) * mm, "end": v(3.18, 1.23) * mm});
            skLineSegment(sketch, "E403", {"start": v(3.18, 1.23) * mm, "end": v(3.44, -0.01) * mm});
            skLineSegment(sketch, "E404", {"start": v(3.44, -0.01) * mm, "end": v(3.18, -1.26) * mm});
            skLineSegment(sketch, "E405", {"start": v(3.18, -1.26) * mm, "end": v(2.5, -2.27) * mm});
            skLineSegment(sketch, "E406", {"start": v(2.5, -2.27) * mm, "end": v(1.47, -2.96) * mm});
            skLineSegment(sketch, "E407", {"start": v(1.47, -2.96) * mm, "end": v(0.2, -3.2) * mm});
            skFitSpline(sketch, "E408", {"points": [v(-17.9, 11.92) * mm, v(-25.09, 8.96) * mm, v(-29.24, 4.5) * mm, v(-29.28, -1.48) * mm, v(-24.98, -6.47) * mm, v(-20.4, -8.3) * mm, v(-19.86, -11.72) * mm, v(-20.43, -17.32) * mm, v(-18.36, -23.38) * mm, v(-14.03, -25.95) * mm, v(-6.7, -24.66) * mm, v(-2.43, -21.84) * mm, v(-0.69, -21.6) * mm, v(4.25, -25.41) * mm, v(12.71, -27.1) * mm, v(16.7, -23.95) * mm, v(18.37, -19.02) * mm, v(18.13, -11.56) * mm, v(20.36, -10.52) * mm, v(25.82, -7.97) * mm, v(29.53, -3.05) * mm, v(28.97, 2.57) * mm, v(23.9, 7.68) * mm, v(18.63, 10.82) * mm, v(19.62, 14.49) * mm, v(18.87, 21.76) * mm, v(14.59, 26.01) * mm, v(8.22, 25.89) * mm, v(0.44, 22.47) * mm, v(-3.76, 25.47) * mm, v(-9.3, 27.5) * mm, v(-14.62, 25.77) * mm, v(-17.75, 20.32) * mm, v(-17.79, 13.03) * mm, v(-17.9, 11.92) * mm]});
            skSolve(sketch);
        }
        {
            var Q0;
            Q0=makeQuery(id+"F0.imprint","IMPRINT",FACE,{"disambiguationData":[TD([[makeQuery(id+"F0.imprint","IMPRINT",EDGE,{"derivedFrom":sQuery(id+"F0.wireOp",EDGE,"E0")}),1.0]])]});
            var Q1;
            Q1=makeQuery(id+"F0.imprint","IMPRINT",FACE,{"disambiguationData":[TD([[makeQuery(id+"F0.imprint","IMPRINT",EDGE,{"derivedFrom":sQuery(id+"F0.wireOp",EDGE,"E380")}),1.0]])]});
            extrude(context, id + "F1", {"entities" : qUnion([Q0, Q1]), "depth" : 2 * mm});
        }
        {
            var Q0;
            Q0=makeQuery(id+"F0.imprint","IMPRINT",FACE,{"disambiguationData":[TD([[makeQuery(id+"F0.imprint","IMPRINT",EDGE,{"derivedFrom":sQuery(id+"F0.wireOp",EDGE,"E0")}),-1.0]])]});
            var Q1;
            Q1=makeQuery(id+"F0.imprint","IMPRINT",FACE,{"disambiguationData":[TD([[makeQuery(id+"F0.imprint","IMPRINT",EDGE,{"derivedFrom":sQuery(id+"F0.wireOp",EDGE,"E392")}),-1.0]])]});
            extrude(context, id + "F2", {"entities" : qUnion([Q0, Q1]), "operationType" : NewBodyOperationType.ADD, "depth" : 5 * mm});
        }
        {
            var Q0;
            Q0=qCreatedBy(makeId("Right.planeOp"),FACE);
            var sketch = newSketch(context, id + "F3", { "sketchPlane" : qUnion([Q0])});
            skLineSegment(sketch, "E409", {"start": v(-27.35, 5) * mm, "end": v(-34.85, 7.5) * mm});
            skLineSegment(sketch, "E410", {"start": v(-34.85, 7.5) * mm, "end": v(-34.85, 10) * mm});
            skLineSegment(sketch, "E411", {"start": v(-34.85, 10) * mm, "end": v(-37.35, 10) * mm});
            skLineSegment(sketch, "E412", {"start": v(-37.35, 10) * mm, "end": v(-37.35, -5) * mm});
            skLineSegment(sketch, "E413", {"start": v(-37.35, -5) * mm, "end": v(-34.85, -5) * mm});
            skLineSegment(sketch, "E414", {"start": v(-34.85, -5) * mm, "end": v(-34.85, -2.5) * mm});
            skLineSegment(sketch, "E415", {"start": v(-34.85, -2.5) * mm, "end": v(-27.35, 0) * mm});
            skLineSegment(sketch, "E416", {"start": v(-27.35, 0) * mm, "end": v(-27.35, 5) * mm});
            skLineSegment(sketch, "E417", {"start": v(-26.35, 0) * mm, "end": v(-27.35, 0) * mm});
            skLineSegment(sketch, "E418", {"start": v(-27.35, 2.5) * mm, "end": v(-37.35, 2.5) * mm});
            skLineSegment(sketch, "E419", {"start": v(-26.35, 0) * mm, "end": v(-26.35, 2) * mm});
            skLineSegment(sketch, "E420", {"start": v(-26.35, 2) * mm, "end": v(-27.35, 2) * mm});
            skSolve(sketch);
        }
        {
            var Q0;
            Q0 = qSketchRegion(id + "F3", true);
            extrude(context, id + "F4", {"entities" : qUnion([Q0]), "operationType" : NewBodyOperationType.ADD, "depth" : 15 * mm, "hasSecondDirection" : true, "secondDirectionOppositeDirection" : true, "secondDirectionDepth" : 10 * mm});
        }
        {
            var Q0;
            Q0=makeQuery(id+"F4.opExtrude","CAP_EDGE",EDGE,{"disambiguationData":[OSD([sQuery(id+"F3.wireOp",EDGE,"E419")])],"isStart":true});
            fillet(context, id + "F5", {"entities" : qUnion([Q0]), "radius" : 5 * mm, "tangentPropagation" : true, "allowEdgeOverflow" : false});
        }
    });
